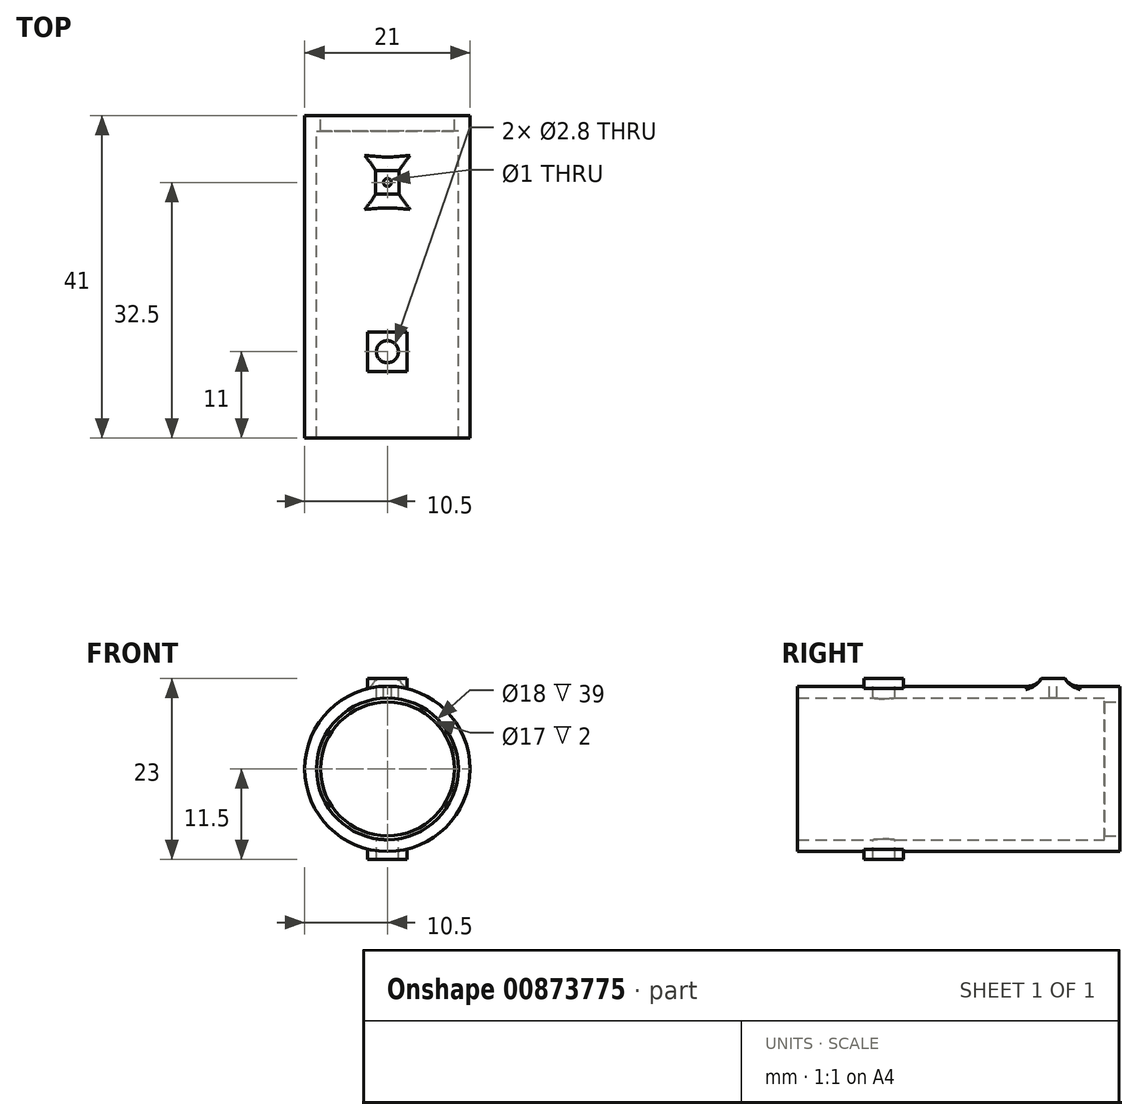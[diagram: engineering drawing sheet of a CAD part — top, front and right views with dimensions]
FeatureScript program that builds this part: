
annotation { "Feature Type Name" : "Feature", "Feature Type Description" : "" }
export const myFeature = defineFeature(function(context is Context, id is Id, definition is map)
    precondition{}
    {
        {
            var Q0;
            Q0=qCreatedBy(makeId("Front.planeOp"),FACE);
            var sketch = newSketch(context, id + "F0", { "sketchPlane" : qUnion([Q0])});
            skCircle(sketch, "E0", {"center": v(0, 0) * mm, "radius": 9 * mm});
            skCircle(sketch, "E1", {"center": v(0, 0) * mm, "radius": 10.5 * mm});
            skLineSegment(sketch, "E2.bottom", {"start": v(-2.5, 11.5) * mm, "end": v(2.5, 11.5) * mm});
            skLineSegment(sketch, "E2.top", {"start": v(-2.5, -11.5) * mm, "end": v(2.5, -11.5) * mm});
            skLineSegment(sketch, "E2.left", {"start": v(-2.5, 11.5) * mm, "end": v(-2.5, -11.5) * mm});
            skLineSegment(sketch, "E2.right", {"start": v(2.5, 11.5) * mm, "end": v(2.5, -11.5) * mm});
            skSolve(sketch);
        }
        {
            var Q0;
            Q0 = qSketchRegion(id + "F0", true);
            extrude(context, id + "F1", {"entities" : qUnion([Q0]), "depth" : 41 * mm, "offsetDistance" : 25 * mm});
        }
        {
            var Q0;
            Q0=makeQuery(id+"F1.opExtrude","SWEPT_FACE",FACE,{"disambiguationData":[OSD([sQuery(id+"F0.wireOp",EDGE,"E2.bottom")])]});
            var sketch = newSketch(context, id + "F2", { "sketchPlane" : qUnion([Q0])});
            skCircle(sketch, "E3", {"center": v(0, -30) * mm, "radius": 1.4 * mm});
            skSolve(sketch);
        }
        {
            var Q0;
            Q0 = qSketchRegion(id + "F2", true);
            extrude(context, id + "F3", {"entities" : qUnion([Q0]), "operationType" : NewBodyOperationType.REMOVE, "oppositeDirection" : true, "depth" : 25 * mm, "offsetDistance" : 25 * mm});
        }
        {
            var Q0;
            Q0=makeQuery(id+"F1.opExtrude","CAP_FACE",FACE,{"disambiguationData":[OSD([sQuery(id+"F0.wireOp",EDGE,"E0"),sQuery(id+"F0.wireOp",EDGE,"E1"),sQuery(id+"F0.wireOp",EDGE,"E2.bottom"),sQuery(id+"F0.wireOp",EDGE,"E2.top"),sQuery(id+"F0.wireOp",EDGE,"E2.left"),sQuery(id+"F0.wireOp",EDGE,"E2.right")])],"isStart":true});
            var sketch = newSketch(context, id + "F4", { "sketchPlane" : qUnion([Q0])});
            skCircle(sketch, "E4", {"center": v(0, 0) * mm, "radius": 8.5 * mm});
            skCircle(sketch, "E5", {"center": v(0, 0) * mm, "radius": 9 * mm});
            skSolve(sketch);
        }
        {
            var Q0;
            Q0=makeQuery(id+"F4.imprint","IMPRINT",FACE,{"disambiguationData":[TD([[makeQuery(id+"F4.imprint","IMPRINT",EDGE,{"derivedFrom":sQuery(id+"F4.wireOp",EDGE,"E4")}),-1.0]])]});
            extrude(context, id + "F5", {"entities" : qUnion([Q0]), "operationType" : NewBodyOperationType.ADD, "depth" : -2 * mm, "offsetDistance" : 25 * mm});
        }
        {
            var Q0;
            Q0=makeQuery(id+"F1.opExtrude","CAP_FACE",FACE,{"disambiguationData":[OSD([sQuery(id+"F0.wireOp",EDGE,"E0"),sQuery(id+"F0.wireOp",EDGE,"E1"),sQuery(id+"F0.wireOp",EDGE,"E2.bottom"),sQuery(id+"F0.wireOp",EDGE,"E2.top"),sQuery(id+"F0.wireOp",EDGE,"E2.left"),sQuery(id+"F0.wireOp",EDGE,"E2.right")])],"isStart":false});
            var sketch = newSketch(context, id + "F6", { "sketchPlane" : qUnion([Q0])});
            skArc(sketch, "E6", {"start": v(-2.5, 10.2) * mm, "mid": v(0, 10.5) * mm, "end": v(2.5, 10.2) * mm});
            skArc(sketch, "E7", {"start": v(2.5, -10.2) * mm, "mid": v(0, -10.5) * mm, "end": v(-2.5, -10.2) * mm});
            skLineSegment(sketch, "E8", {"start": v(-2.5, 10.2) * mm, "end": v(-2.5, 11.5) * mm});
            skLineSegment(sketch, "E9", {"start": v(-2.5, 11.5) * mm, "end": v(2.5, 11.5) * mm});
            skLineSegment(sketch, "E10", {"start": v(2.5, 11.5) * mm, "end": v(2.5, 10.2) * mm});
            skLineSegment(sketch, "E11", {"start": v(2.5, -10.2) * mm, "end": v(2.5, -11.5) * mm});
            skLineSegment(sketch, "E12", {"start": v(2.5, -11.5) * mm, "end": v(-2.5, -11.5) * mm});
            skLineSegment(sketch, "E13", {"start": v(-2.5, -11.5) * mm, "end": v(-2.5, -10.2) * mm});
            skSolve(sketch);
        }
        {
            var Q0;
            Q0 = qSketchRegion(id + "F6", true);
            extrude(context, id + "F7", {"entities" : qUnion([Q0]), "operationType" : NewBodyOperationType.REMOVE, "oppositeDirection" : true, "depth" : 8.5 * mm, "offsetDistance" : 25 * mm});
        }
        {
            var Q0;
            Q0=makeQuery(id+"F5.boolean.opBoolean","MERGE",FACE,{"derivedFrom":[makeQuery(id+"F1.opExtrude","CAP_FACE",FACE,{"disambiguationData":[OSD([sQuery(id+"F0.wireOp",EDGE,"E0"),sQuery(id+"F0.wireOp",EDGE,"E1"),sQuery(id+"F0.wireOp",EDGE,"E2.bottom"),sQuery(id+"F0.wireOp",EDGE,"E2.top"),sQuery(id+"F0.wireOp",EDGE,"E2.left"),sQuery(id+"F0.wireOp",EDGE,"E2.right")])],"isStart":true}),makeQuery(id+"F5.opExtrude","CAP_FACE",FACE,{"disambiguationData":[OSD([sQuery(id+"F4.wireOp",EDGE,"E4"),sQuery(id+"F4.wireOp",EDGE,"E5")])],"isStart":true})]});
            var sketch = newSketch(context, id + "F8", { "sketchPlane" : qUnion([Q0])});
            skArc(sketch, "E14", {"start": v(-2.5, 10.2) * mm, "mid": v(0, 10.5) * mm, "end": v(2.5, 10.2) * mm});
            skArc(sketch, "E15", {"start": v(-2.5, -10.2) * mm, "mid": v(0, -10.5) * mm, "end": v(2.5, -10.2) * mm});
            skLineSegment(sketch, "E16", {"start": v(-2.5, 10.2) * mm, "end": v(-2.5, 11.5) * mm});
            skLineSegment(sketch, "E17", {"start": v(-2.5, 11.5) * mm, "end": v(2.5, 11.5) * mm});
            skLineSegment(sketch, "E18", {"start": v(2.5, 11.5) * mm, "end": v(2.5, 10.2) * mm});
            skLineSegment(sketch, "E19", {"start": v(2.5, -10.2) * mm, "end": v(2.5, -11.5) * mm});
            skLineSegment(sketch, "E20", {"start": v(2.5, -11.5) * mm, "end": v(-2.5, -11.5) * mm});
            skLineSegment(sketch, "E21", {"start": v(-2.5, -11.5) * mm, "end": v(-2.5, -10.2) * mm});
            skSolve(sketch);
        }
        {
            var Q0;
            Q0 = qSketchRegion(id + "F8", true);
            extrude(context, id + "F9", {"entities" : qUnion([Q0]), "operationType" : NewBodyOperationType.REMOVE, "oppositeDirection" : true, "depth" : 27.5 * mm, "offsetDistance" : 25 * mm});
        }
        {
            var Q0;
            Q0=qCreatedBy(makeId("Top.planeOp"),FACE);
            cPlane(context, id + "F10", {"entities" : qUnion([Q0]), "cplaneType" : CPlaneType.OFFSET, "offset" : 10.5 * mm, "width" : 150 * mm, "height" : 150 * mm});
        }
        {
            var Q0;
            Q0=qCreatedBy(id+"F10.planeOp",FACE);
            var sketch = newSketch(context, id + "F11", { "sketchPlane" : qUnion([Q0])});
            skLineSegment(sketch, "E22.bottom", {"start": v(1.5, -10) * mm, "end": v(-1.5, -10) * mm});
            skLineSegment(sketch, "E22.top", {"start": v(1.5, -7) * mm, "end": v(-1.5, -7) * mm});
            skLineSegment(sketch, "E22.left", {"start": v(1.5, -10) * mm, "end": v(1.5, -7) * mm});
            skLineSegment(sketch, "E22.right", {"start": v(-1.5, -10) * mm, "end": v(-1.5, -7) * mm});
            skSolve(sketch);
        }
        {
            var Q0;
            Q0 = qSketchRegion(id + "F11", true);
            extrude(context, id + "F12", {"entities" : qUnion([Q0]), "operationType" : NewBodyOperationType.ADD, "depth" : 1 * mm, "offsetDistance" : 25 * mm, "hasSecondDirection" : true, "secondDirectionOppositeDirection" : true, "secondDirectionDepth" : 1 * mm});
        }
        {
            var Q0;
            Q0=makeQuery(id+"F12.opExtrude","CAP_FACE",FACE,{"disambiguationData":[OSD([sQuery(id+"F11.wireOp",EDGE,"E22.bottom"),sQuery(id+"F11.wireOp",EDGE,"E22.top"),sQuery(id+"F11.wireOp",EDGE,"E22.left"),sQuery(id+"F11.wireOp",EDGE,"E22.right")])],"isStart":false});
            var sketch = newSketch(context, id + "F13", { "sketchPlane" : qUnion([Q0])});
            skCircle(sketch, "E23", {"center": v(0, -8.5) * mm, "radius": 0.5 * mm});
            skSolve(sketch);
        }
        {
            var Q0;
            {var subQ0=sQuery(id+"F0.wireOp",EDGE,"E2.right");var subQ1=sQuery(id+"F0.wireOp",EDGE,"E1");var subQ2=sQuery(id+"F0.wireOp",EDGE,"E2.left");Q0=makeQuery(id+"F12.boolean.opBoolean","INTERSECT",EDGE,{"derivedFrom":[makeQuery(id+"F9.boolean.opBoolean","MERGE",FACE,{"derivedFrom":[makeQuery(id+"F7.boolean.opBoolean","MERGE",FACE,{"derivedFrom":[makeQuery(id+"F1.opExtrude","SWEPT_FACE",FACE,{"disambiguationData":[OSD([subQ1]),TDD([makeQuery(id+"F0.imprint","IMPRINT",EDGE,{"disambiguationData":[TD([[makeQuery(id+"F0.imprint","INTERSECT",VERTEX,{"disambiguationData":[OD(0.0)],"derivedFrom":[subQ1,subQ2]}),-1.0]])],"derivedFrom":subQ1})])]}),makeQuery(id+"F1.opExtrude","SWEPT_FACE",FACE,{"disambiguationData":[OSD([subQ1]),TDD([makeQuery(id+"F0.imprint","IMPRINT",EDGE,{"disambiguationData":[TD([[makeQuery(id+"F0.imprint","INTERSECT",VERTEX,{"disambiguationData":[OD(0.0)],"derivedFrom":[subQ1,subQ0]}),1.0]])],"derivedFrom":subQ1})])]})],"fromTools":[makeQuery(id+"F7.opExtrude","SWEPT_FACE",FACE,{"disambiguationData":[OSD([sQuery(id+"F6.wireOp",EDGE,"E6")])]}),makeQuery(id+"F7.opExtrude","SWEPT_FACE",FACE,{"disambiguationData":[OSD([sQuery(id+"F6.wireOp",EDGE,"E7")])]})]})],"fromTools":[makeQuery(id+"F9.opExtrude","SWEPT_FACE",FACE,{"disambiguationData":[OSD([sQuery(id+"F8.wireOp",EDGE,"E14")])]}),makeQuery(id+"F9.opExtrude","SWEPT_FACE",FACE,{"disambiguationData":[OSD([sQuery(id+"F8.wireOp",EDGE,"E15")])]})]}),makeQuery(id+"F12.opExtrude","SWEPT_FACE",FACE,{"disambiguationData":[OSD([sQuery(id+"F11.wireOp",EDGE,"E22.left")])]})]});}
            var Q1;
            {var subQ0=sQuery(id+"F0.wireOp",EDGE,"E2.right");var subQ1=sQuery(id+"F0.wireOp",EDGE,"E1");var subQ2=sQuery(id+"F0.wireOp",EDGE,"E2.left");Q1=makeQuery(id+"F12.boolean.opBoolean","INTERSECT",EDGE,{"derivedFrom":[makeQuery(id+"F9.boolean.opBoolean","MERGE",FACE,{"derivedFrom":[makeQuery(id+"F7.boolean.opBoolean","MERGE",FACE,{"derivedFrom":[makeQuery(id+"F1.opExtrude","SWEPT_FACE",FACE,{"disambiguationData":[OSD([subQ1]),TDD([makeQuery(id+"F0.imprint","IMPRINT",EDGE,{"disambiguationData":[TD([[makeQuery(id+"F0.imprint","INTERSECT",VERTEX,{"disambiguationData":[OD(0.0)],"derivedFrom":[subQ1,subQ2]}),-1.0]])],"derivedFrom":subQ1})])]}),makeQuery(id+"F1.opExtrude","SWEPT_FACE",FACE,{"disambiguationData":[OSD([subQ1]),TDD([makeQuery(id+"F0.imprint","IMPRINT",EDGE,{"disambiguationData":[TD([[makeQuery(id+"F0.imprint","INTERSECT",VERTEX,{"disambiguationData":[OD(0.0)],"derivedFrom":[subQ1,subQ0]}),1.0]])],"derivedFrom":subQ1})])]})],"fromTools":[makeQuery(id+"F7.opExtrude","SWEPT_FACE",FACE,{"disambiguationData":[OSD([sQuery(id+"F6.wireOp",EDGE,"E6")])]}),makeQuery(id+"F7.opExtrude","SWEPT_FACE",FACE,{"disambiguationData":[OSD([sQuery(id+"F6.wireOp",EDGE,"E7")])]})]})],"fromTools":[makeQuery(id+"F9.opExtrude","SWEPT_FACE",FACE,{"disambiguationData":[OSD([sQuery(id+"F8.wireOp",EDGE,"E14")])]}),makeQuery(id+"F9.opExtrude","SWEPT_FACE",FACE,{"disambiguationData":[OSD([sQuery(id+"F8.wireOp",EDGE,"E15")])]})]}),makeQuery(id+"F12.opExtrude","SWEPT_FACE",FACE,{"disambiguationData":[OSD([sQuery(id+"F11.wireOp",EDGE,"E22.right")])]})]});}
            var Q2;
            {var subQ0=sQuery(id+"F0.wireOp",EDGE,"E2.right");var subQ1=sQuery(id+"F0.wireOp",EDGE,"E1");var subQ2=sQuery(id+"F0.wireOp",EDGE,"E2.left");Q2=makeQuery(id+"F12.boolean.opBoolean","INTERSECT",EDGE,{"derivedFrom":[makeQuery(id+"F9.boolean.opBoolean","MERGE",FACE,{"derivedFrom":[makeQuery(id+"F7.boolean.opBoolean","MERGE",FACE,{"derivedFrom":[makeQuery(id+"F1.opExtrude","SWEPT_FACE",FACE,{"disambiguationData":[OSD([subQ1]),TDD([makeQuery(id+"F0.imprint","IMPRINT",EDGE,{"disambiguationData":[TD([[makeQuery(id+"F0.imprint","INTERSECT",VERTEX,{"disambiguationData":[OD(0.0)],"derivedFrom":[subQ1,subQ2]}),-1.0]])],"derivedFrom":subQ1})])]}),makeQuery(id+"F1.opExtrude","SWEPT_FACE",FACE,{"disambiguationData":[OSD([subQ1]),TDD([makeQuery(id+"F0.imprint","IMPRINT",EDGE,{"disambiguationData":[TD([[makeQuery(id+"F0.imprint","INTERSECT",VERTEX,{"disambiguationData":[OD(0.0)],"derivedFrom":[subQ1,subQ0]}),1.0]])],"derivedFrom":subQ1})])]})],"fromTools":[makeQuery(id+"F7.opExtrude","SWEPT_FACE",FACE,{"disambiguationData":[OSD([sQuery(id+"F6.wireOp",EDGE,"E6")])]}),makeQuery(id+"F7.opExtrude","SWEPT_FACE",FACE,{"disambiguationData":[OSD([sQuery(id+"F6.wireOp",EDGE,"E7")])]})]})],"fromTools":[makeQuery(id+"F9.opExtrude","SWEPT_FACE",FACE,{"disambiguationData":[OSD([sQuery(id+"F8.wireOp",EDGE,"E14")])]}),makeQuery(id+"F9.opExtrude","SWEPT_FACE",FACE,{"disambiguationData":[OSD([sQuery(id+"F8.wireOp",EDGE,"E15")])]})]}),makeQuery(id+"F12.opExtrude","SWEPT_FACE",FACE,{"disambiguationData":[OSD([sQuery(id+"F11.wireOp",EDGE,"E22.top")])]})]});}
            var Q3;
            {var subQ0=sQuery(id+"F0.wireOp",EDGE,"E2.right");var subQ1=sQuery(id+"F0.wireOp",EDGE,"E1");var subQ2=sQuery(id+"F0.wireOp",EDGE,"E2.left");Q3=makeQuery(id+"F12.boolean.opBoolean","INTERSECT",EDGE,{"derivedFrom":[makeQuery(id+"F9.boolean.opBoolean","MERGE",FACE,{"derivedFrom":[makeQuery(id+"F7.boolean.opBoolean","MERGE",FACE,{"derivedFrom":[makeQuery(id+"F1.opExtrude","SWEPT_FACE",FACE,{"disambiguationData":[OSD([subQ1]),TDD([makeQuery(id+"F0.imprint","IMPRINT",EDGE,{"disambiguationData":[TD([[makeQuery(id+"F0.imprint","INTERSECT",VERTEX,{"disambiguationData":[OD(0.0)],"derivedFrom":[subQ1,subQ2]}),-1.0]])],"derivedFrom":subQ1})])]}),makeQuery(id+"F1.opExtrude","SWEPT_FACE",FACE,{"disambiguationData":[OSD([subQ1]),TDD([makeQuery(id+"F0.imprint","IMPRINT",EDGE,{"disambiguationData":[TD([[makeQuery(id+"F0.imprint","INTERSECT",VERTEX,{"disambiguationData":[OD(0.0)],"derivedFrom":[subQ1,subQ0]}),1.0]])],"derivedFrom":subQ1})])]})],"fromTools":[makeQuery(id+"F7.opExtrude","SWEPT_FACE",FACE,{"disambiguationData":[OSD([sQuery(id+"F6.wireOp",EDGE,"E6")])]}),makeQuery(id+"F7.opExtrude","SWEPT_FACE",FACE,{"disambiguationData":[OSD([sQuery(id+"F6.wireOp",EDGE,"E7")])]})]})],"fromTools":[makeQuery(id+"F9.opExtrude","SWEPT_FACE",FACE,{"disambiguationData":[OSD([sQuery(id+"F8.wireOp",EDGE,"E14")])]}),makeQuery(id+"F9.opExtrude","SWEPT_FACE",FACE,{"disambiguationData":[OSD([sQuery(id+"F8.wireOp",EDGE,"E15")])]})]}),makeQuery(id+"F12.opExtrude","SWEPT_FACE",FACE,{"disambiguationData":[OSD([sQuery(id+"F11.wireOp",EDGE,"E22.bottom")])]})]});}
            fillet(context, id + "F14", {"entities" : qUnion([Q0, Q1, Q2, Q3]), "radius" : 2 * mm, "tangentPropagation" : true, "allowEdgeOverflow" : false});
        }
        {
            var Q0;
            Q0 = qSketchRegion(id + "F13", true);
            extrude(context, id + "F15", {"entities" : qUnion([Q0]), "operationType" : NewBodyOperationType.REMOVE, "oppositeDirection" : true, "depth" : 3 * mm, "offsetDistance" : 25 * mm});
        }
    });
